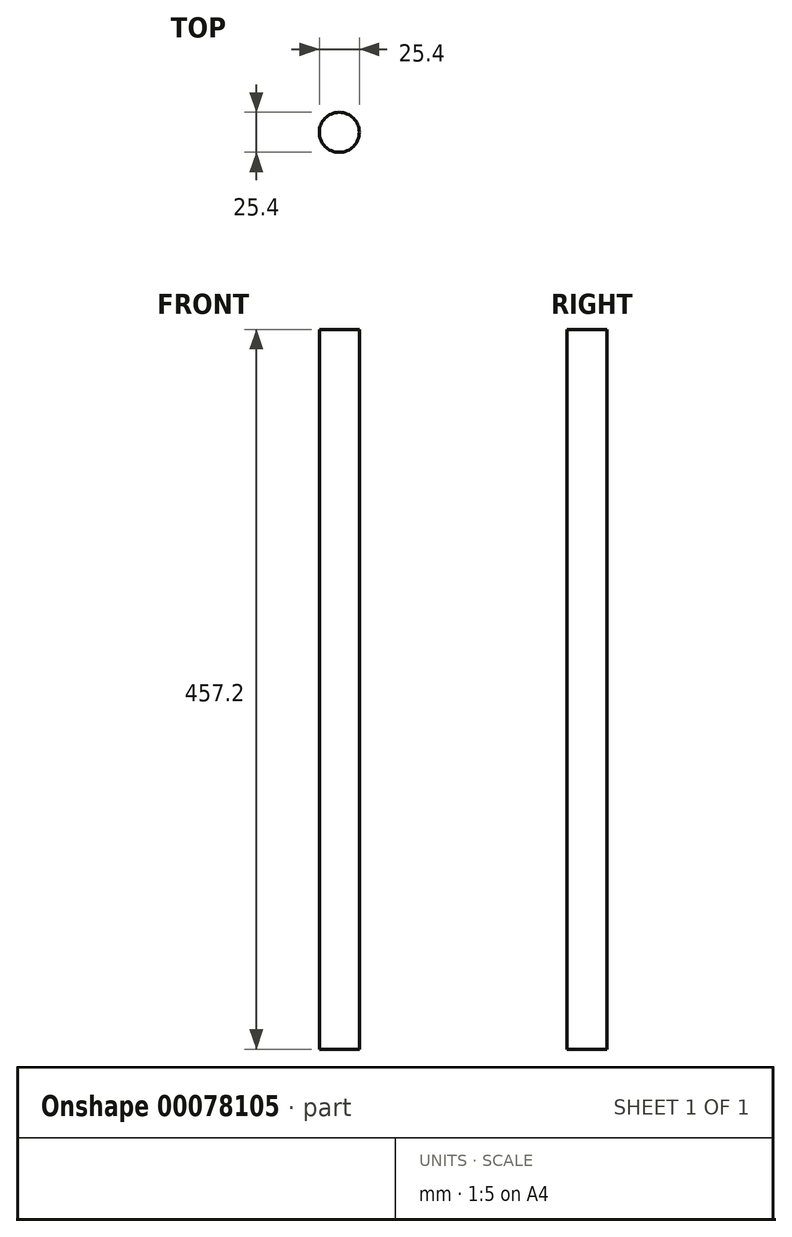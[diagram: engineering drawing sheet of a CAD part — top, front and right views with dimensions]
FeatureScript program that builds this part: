
annotation { "Feature Type Name" : "Feature", "Feature Type Description" : "" }
export const myFeature = defineFeature(function(context is Context, id is Id, definition is map)
    precondition{}
    {
        {
            var Q0;
            Q0=qCreatedBy(makeId("Top.planeOp"),FACE);
            var sketch = newSketch(context, id + "F0", { "sketchPlane" : qUnion([Q0])});
            skCircle(sketch, "E0", {"center": v(-6.03, 6.15) * mm, "radius": 12.7 * mm});
            skSolve(sketch);
        }
        {
            var Q0;
            Q0=makeQuery(id+"F0.imprint","IMPRINT",FACE,{"disambiguationData":[TD([[makeQuery(id+"F0.imprint","IMPRINT",EDGE,{"derivedFrom":sQuery(id+"F0.wireOp",EDGE,"E0")}),1.0]])]});
            extrude(context, id + "F1", {"entities" : qUnion([Q0]), "depth" : 457.2 * mm});
        }
    });
